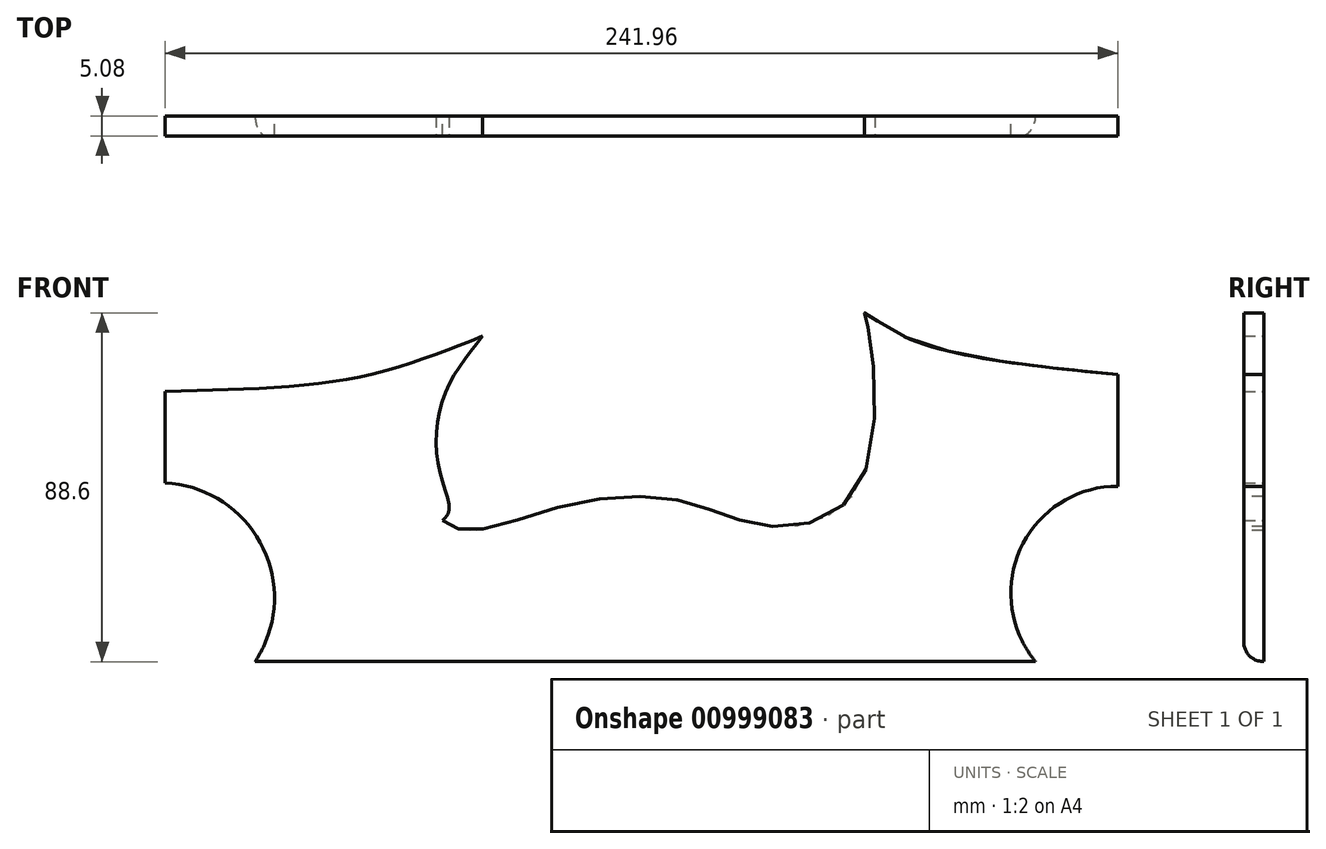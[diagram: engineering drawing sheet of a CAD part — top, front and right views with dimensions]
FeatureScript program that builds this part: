
annotation { "Feature Type Name" : "Feature", "Feature Type Description" : "" }
export const myFeature = defineFeature(function(context is Context, id is Id, definition is map)
    precondition{}
    {
        {
            var Q0;
            Q0=qCreatedBy(makeId("Front.planeOp"),FACE);
            var sketch = newSketch(context, id + "F0", { "sketchPlane" : qUnion([Q0])});
            skLineSegment(sketch, "E0", {"start": v(-88.8, 11.34) * mm, "end": v(-88.8, 2.75) * mm});
            skFitSpline(sketch, "E1", {"points": [v(-88.8, 11.34) * mm, v(-41.48, 14.71) * mm, v(-8.19, 25.46) * mm], "startDerivative": vector(92.2, 3.55) * mm, "endDerivative": vector(68.42, 26.87) * mm});
            skFitSpline(sketch, "E2", {"points": [v(-8.19, 25.46) * mm, v(-17.55, 11.34) * mm, v(-19.46, -7.3) * mm, v(-16.68, -18.57) * mm, v(-18.42, -21.35) * mm], "startDerivative": vector(-34.97, -45.72) * mm, "endDerivative": vector(-18.14, -17.04) * mm});
            skFitSpline(sketch, "E3", {"points": [v(-18.42, -21.35) * mm, v(-11.66, -23.95) * mm, v(14.35, -17.19) * mm, v(44.17, -16.84) * mm, v(63.93, -22.74) * mm, v(87.51, -12.33) * mm, v(89.42, 28.76) * mm, v(88.9, 31.36) * mm, v(98.6, 25.46) * mm, v(153.15, 15.68) * mm], "startDerivative": vector(87.3, -59.69) * mm, "endDerivative": vector(360.36, -36.98) * mm});
            skLineSegment(sketch, "E4", {"start": v(153.15, 15.68) * mm, "end": v(153.15, 5.16) * mm});
            skLineSegment(sketch, "E5", {"start": v(-61.46, -57.24) * mm, "end": v(126.3, -57.24) * mm});
            skLineSegment(sketch, "E6", {"start": v(-88.8, 2.75) * mm, "end": v(-88.8, -11.84) * mm});
            skLineSegment(sketch, "E7", {"start": v(153.15, 5.16) * mm, "end": v(153.15, -12.66) * mm});
            skLineSegment(sketch, "E8", {"start": v(-61.46, -57.24) * mm, "end": v(-66.01, -57.24) * mm});
            skLineSegment(sketch, "E9", {"start": v(126.3, -57.24) * mm, "end": v(132.3, -57.24) * mm});
            skArc(sketch, "E10", {"start": v(-66.01, -57.24) * mm, "mid": v(-64.2, -27.9) * mm, "end": v(-88.8, -11.84) * mm});
            skArc(sketch, "E11", {"start": v(153.15, -12.66) * mm, "mid": v(128.54, -28.32) * mm, "end": v(132.3, -57.24) * mm});
            skPoint(sketch, "E12.orphan", {"position": v(153.15, -57.24) * mm});
            skPoint(sketch, "E13.orphan", {"position": v(153.15, -22.42) * mm});
            skLineSegment(sketch, "E14", {"start": v(-66.01, -57.24) * mm, "end": v(-125.53, -57.24) * mm});
            skPoint(sketch, "E15.orphan", {"position": v(-88.8, -11.52) * mm});
            skSolve(sketch);
        }
        {
            var Q0;
            Q0=makeQuery(id+"F0.imprint","IMPRINT",FACE,{"disambiguationData":[TD([[makeQuery(id+"F0.imprint","IMPRINT",EDGE,{"derivedFrom":sQuery(id+"F0.wireOp",EDGE,"E0")}),1.0]])]});
            extrude(context, id + "F1", {"entities" : qUnion([Q0]), "depth" : 5.08 * mm, "offsetDistance" : 25.4 * mm});
        }
        {
            var Q0;
            Q0=makeQuery(id+"F1.opExtrude","CAP_EDGE",EDGE,{"disambiguationData":[OSD([sQuery(id+"F0.wireOp",EDGE,"E5")])],"isStart":false});
            fillet(context, id + "F2", {"entities" : qUnion([Q0]), "radius" : 5.08 * mm, "allowEdgeOverflow" : false});
        }
    });
